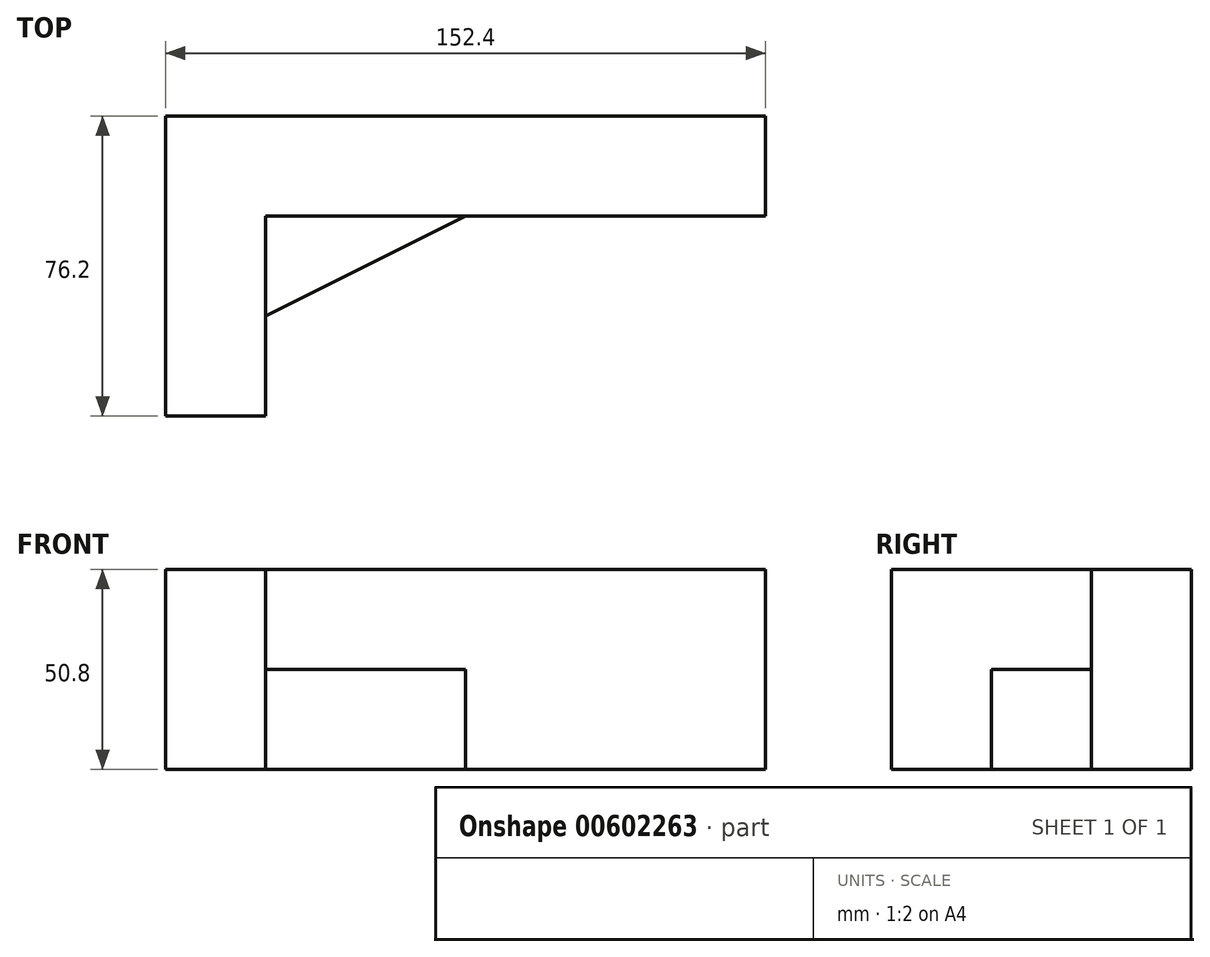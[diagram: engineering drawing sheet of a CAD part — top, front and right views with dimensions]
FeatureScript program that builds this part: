
annotation { "Feature Type Name" : "Feature", "Feature Type Description" : "" }
export const myFeature = defineFeature(function(context is Context, id is Id, definition is map)
    precondition{}
    {
        {
            var Q0;
            Q0=qCreatedBy(makeId("Front.planeOp"),FACE);
            var sketch = newSketch(context, id + "F0", { "sketchPlane" : qUnion([Q0])});
            skLineSegment(sketch, "E0", {"start": v(0, 0) * mm, "end": v(0, 50.8) * mm});
            skLineSegment(sketch, "E1", {"start": v(0, 50.8) * mm, "end": v(152.4, 50.8) * mm});
            skLineSegment(sketch, "E2", {"start": v(152.4, 50.8) * mm, "end": v(152.4, 0) * mm});
            skLineSegment(sketch, "E3", {"start": v(152.4, 0) * mm, "end": v(0, 0) * mm});
            skLineSegment(sketch, "E4", {"start": v(25.4, 0) * mm, "end": v(25.4, 50.8) * mm});
            skLineSegment(sketch, "E5", {"start": v(0, 0) * mm, "end": v(25.4, 0) * mm});
            skSolve(sketch);
        }
        {
            var Q0;
            {var subQ0=sQuery(id+"F0.wireOp",EDGE,"E2");Q0=makeQuery(id+"F0.imprint","IMPRINT",FACE,{"disambiguationData":[TD([[makeQuery(id+"F0.imprint","IMPRINT",EDGE,{"derivedFrom":subQ0}),-1.0]])]});}
            var Q1;
            {var subQ0=sQuery(id+"F0.wireOp",EDGE,"E0");Q1=makeQuery(id+"F0.imprint","IMPRINT",FACE,{"disambiguationData":[TD([[makeQuery(id+"F0.imprint","IMPRINT",EDGE,{"derivedFrom":subQ0}),-1.0]])]});}
            extrude(context, id + "F1", {"entities" : qUnion([Q0, Q1]), "oppositeDirection" : true, "depth" : 76.2 * mm, "offsetDistance" : 25.4 * mm});
        }
        {
            var Q0;
            Q0=makeQuery(id+"F1.opExtrude","SWEPT_FACE",FACE,{"disambiguationData":[OSD([sQuery(id+"F0.wireOp",EDGE,"E1")])]});
            var sketch = newSketch(context, id + "F2", { "sketchPlane" : qUnion([Q0])});
            skLineSegment(sketch, "E6", {"start": v(25.4, 0) * mm, "end": v(25.4, 50.8) * mm});
            skLineSegment(sketch, "E7", {"start": v(25.4, 50.8) * mm, "end": v(152.4, 50.8) * mm});
            skLineSegment(sketch, "E8", {"start": v(152.4, 50.8) * mm, "end": v(152.4, 0) * mm});
            skLineSegment(sketch, "E9", {"start": v(152.4, 0) * mm, "end": v(25.4, 0) * mm});
            skSolve(sketch);
        }
        {
            var Q0;
            Q0=makeQuery(id+"F2.imprint","IMPRINT",FACE,{"disambiguationData":[TD([[makeQuery(id+"F2.imprint","IMPRINT",EDGE,{"derivedFrom":sQuery(id+"F2.wireOp",EDGE,"E6")}),-1.0]])]});
            extrude(context, id + "F3", {"entities" : qUnion([Q0]), "operationType" : NewBodyOperationType.REMOVE, "oppositeDirection" : true, "depth" : 50.8 * mm, "offsetDistance" : 25.4 * mm});
        }
        {
            var Q0;
            Q0=makeQuery(id+"F3.boolean.opBoolean","COPY",FACE,{"derivedFrom":makeQuery(id+"F3.opExtrude","SWEPT_FACE",FACE,{"disambiguationData":[OSD([sQuery(id+"F2.wireOp",EDGE,"E7")])]})});
            var sketch = newSketch(context, id + "F4", { "sketchPlane" : qUnion([Q0])});
            skLineSegment(sketch, "E10", {"start": v(25.4, 0) * mm, "end": v(76.2, 0) * mm});
            skLineSegment(sketch, "E11", {"start": v(76.2, 0) * mm, "end": v(76.2, 25.4) * mm});
            skLineSegment(sketch, "E12", {"start": v(76.2, 25.4) * mm, "end": v(25.4, 25.4) * mm});
            skLineSegment(sketch, "E13", {"start": v(25.4, 25.4) * mm, "end": v(25.4, 0) * mm});
            skSolve(sketch);
        }
        {
            var Q0;
            Q0=makeQuery(id+"F4.imprint","IMPRINT",FACE,{"disambiguationData":[TD([[makeQuery(id+"F4.imprint","IMPRINT",EDGE,{"derivedFrom":sQuery(id+"F4.wireOp",EDGE,"E10")}),1.0]])]});
            extrude(context, id + "F5", {"entities" : qUnion([Q0]), "operationType" : NewBodyOperationType.ADD, "depth" : 25.4 * mm, "offsetDistance" : 25.4 * mm});
        }
        {
            var Q0;
            Q0=makeQuery(id+"F5.opExtrude","SWEPT_FACE",FACE,{"disambiguationData":[OSD([sQuery(id+"F4.wireOp",EDGE,"E12")])]});
            var sketch = newSketch(context, id + "F6", { "sketchPlane" : qUnion([Q0])});
            skLineSegment(sketch, "E14", {"start": v(25.4, 25.4) * mm, "end": v(76.2, 50.8) * mm});
            skSolve(sketch);
        }
        {
            var Q0;
            Q0=makeQuery(id+"F6.imprint","IMPRINT",FACE,{"disambiguationData":[TD([[makeQuery(id+"F6.imprint","IMPRINT",EDGE,{"derivedFrom":sQuery(id+"F6.wireOp",EDGE,"E14")}),-1.0]])]});
            extrude(context, id + "F7", {"entities" : qUnion([Q0]), "operationType" : NewBodyOperationType.REMOVE, "oppositeDirection" : true, "depth" : 25.4 * mm, "offsetDistance" : 25.4 * mm});
        }
    });
